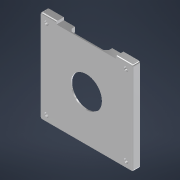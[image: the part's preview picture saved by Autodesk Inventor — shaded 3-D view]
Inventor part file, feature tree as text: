
AUTODESK INVENTOR PART (.ipt)
format: ipt  version: 2022 (Build 260153000, 153)  size: 174,080 bytes
history: native  units: mm
features: sketch x3, other x3, extrude x2, reference x2, hole x1, chamfer x1, fillet x1, projected_geometry x1
ambient origin geometry x8: Origin, YZ Plane, XZ Plane, XY Plane, X Axis, Y Axis, Z Axis, Center Point
bodies: Solid1 (feature_tree)
feature tree (14):
  extrude  "Extrusion1"  Depth=2.0mm TaperAngle=0.0deg
  extrude  "Extrusion2"  Depth=1.0mm
  hole  "Hole1"  [1 undecoded]
  chamfer  "Chamfer1"  Distance=2.0mm
  fillet  "Fillet1"  [1 undecoded]
  sketch  "Sketch1"  dims[d0=9.0mm d1=0.0mm d2=2.0mm d3=0.0mm]
  reference  "Reference1"
  sketch  "Sketch2"  dims[d4=1.0mm d5=120.0mm]
  projected_geometry  "Projected Loop1"
  reference  "Reference2"
  sketch  "Sketch3"  dims[d7=3.4mm d8=6.0mm d9=6.5mm d10=3.4mm d11=90.0deg d12=8.8mm d13=20.594885mm d14=4.0mm d15=2.0mm d16=45.0deg d17=2.0mm]
  other  "SistemaElevacionV2.iam"
  other  "Soporte:1"
  other  "BridaTornillo2:1"
note: 2 required parameter values undecoded (feature->parameter linkage not recoverable at this tier; creation-order binding heuristic only, values carry confidence <= 0.55)
